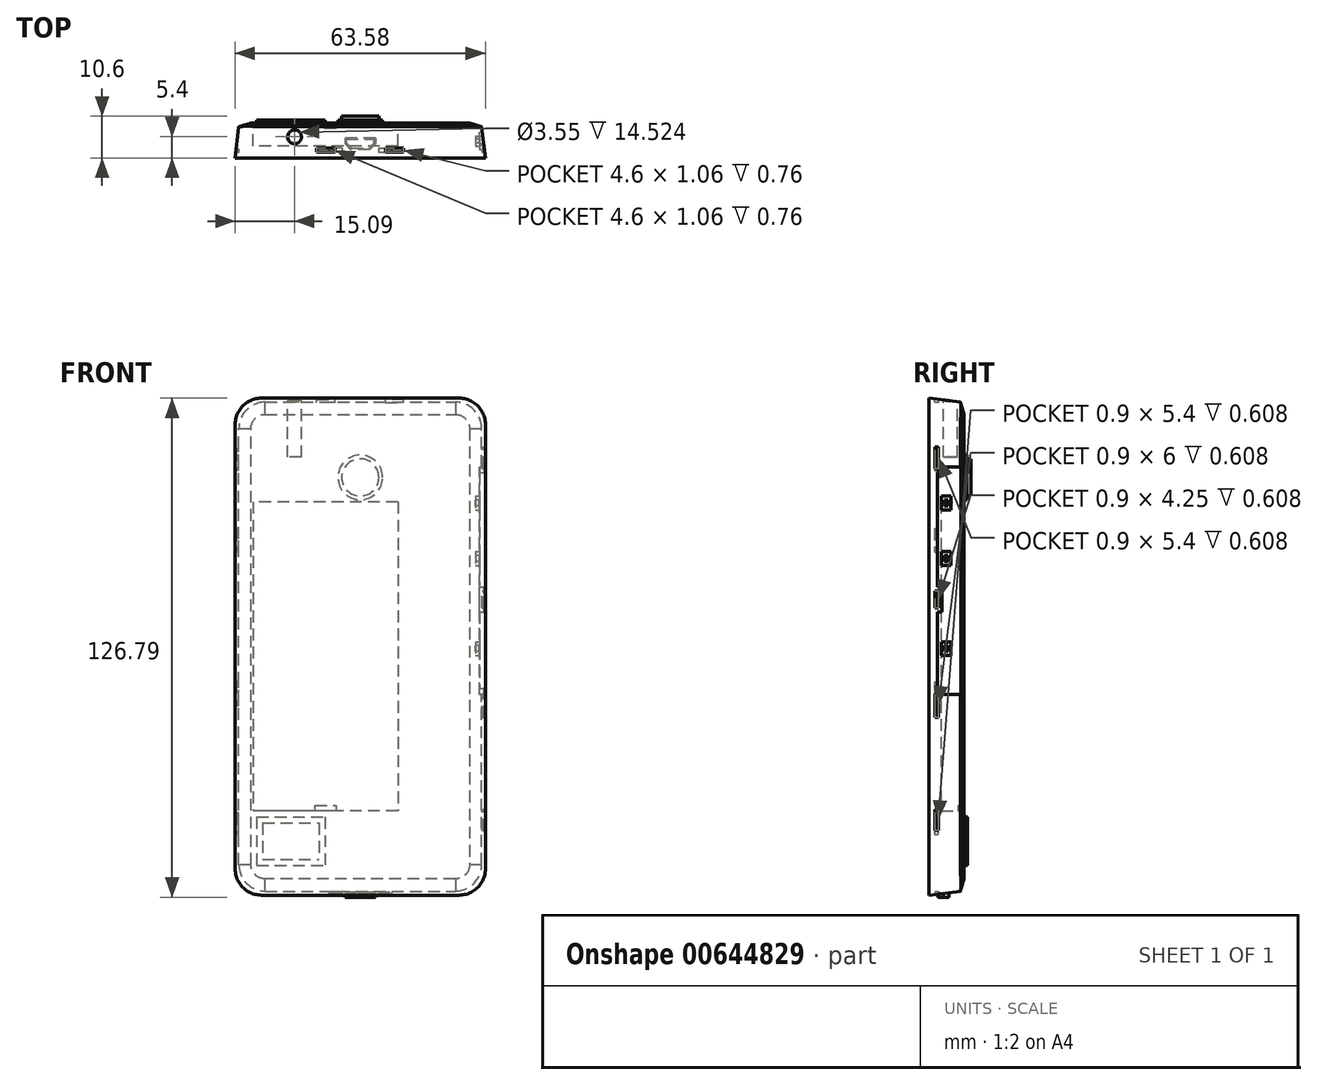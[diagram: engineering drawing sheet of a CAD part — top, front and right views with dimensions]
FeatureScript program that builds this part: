
annotation { "Feature Type Name" : "Feature", "Feature Type Description" : "" }
export const myFeature = defineFeature(function(context is Context, id is Id, definition is map)
    precondition{}
    {
        {
            var Q0;
            Q0=qCreatedBy(makeId("Front.planeOp"),FACE);
            cPlane(context, id + "F0", {"entities" : qUnion([Q0]), "cplaneType" : CPlaneType.OFFSET, "offset" : 9 * mm, "width" : 150 * mm, "height" : 150 * mm});
        }
        {
            var Q0;
            Q0=qCreatedBy(id+"F0.planeOp",FACE);
            var sketch = newSketch(context, id + "F1", { "sketchPlane" : qUnion([Q0])});
            skLineSegment(sketch, "E0.bottom", {"start": v(31.8, 63.15) * mm, "end": v(-31.8, 63.15) * mm});
            skLineSegment(sketch, "E0.top", {"start": v(31.8, -63.15) * mm, "end": v(-31.8, -63.15) * mm});
            skLineSegment(sketch, "E0.left", {"start": v(31.8, 63.15) * mm, "end": v(31.8, -63.15) * mm});
            skLineSegment(sketch, "E0.right", {"start": v(-31.8, 63.15) * mm, "end": v(-31.8, -63.15) * mm});
            skPoint(sketch, "E0.middle", {"position": v(0, 0) * mm});
            skLineSegment(sketch, "E1", {"start": v(0, -63.15) * mm, "end": v(0, -63.65) * mm, "construction": true});
            skPoint(sketch, "E1.endSnap0", {"position": v(0, -63.15) * mm});
            skSolve(sketch);
        }
        {
            var Q0;
            Q0=qCreatedBy(makeId("Front.planeOp"),FACE);
            var sketch = newSketch(context, id + "F2", { "sketchPlane" : qUnion([Q0])});
            skLineSegment(sketch, "E2.bottom", {"start": v(30.75, 62) * mm, "end": v(-30.75, 62) * mm});
            skLineSegment(sketch, "E2.top", {"start": v(30.75, -62) * mm, "end": v(-30.75, -62) * mm});
            skLineSegment(sketch, "E2.left", {"start": v(30.75, 62) * mm, "end": v(30.75, -62) * mm});
            skLineSegment(sketch, "E2.right", {"start": v(-30.75, 62) * mm, "end": v(-30.75, -62) * mm});
            skPoint(sketch, "E2.middle", {"position": v(0, 0) * mm});
            skSolve(sketch);
        }
        {
            var Q0;
            Q0=qSketchRegion(id+"F1",true);
            var Q1;
            Q1=qSketchRegion(id+"F2",true);
            loft(context, id + "F3", {"sheetProfilesArray" : [{ "sheetProfileEntities" : qUnion([Q0]) }, { "sheetProfileEntities" : qUnion([Q1]) }]});
        }
        {
            var Q0;
            Q0=makeQuery(id+"F3.opLoft","CAP_FACE",FACE,{"disambiguationData":[OSD([makeQuery(id+"F2.imprint","IMPRINT",FACE,{"disambiguationData":[TD([[makeQuery(id+"F2.imprint","IMPRINT",EDGE,{"derivedFrom":sQuery(id+"F2.wireOp",EDGE,"E2.bottom")}),1.0]])]})])],"isStart":true});
            var sketch = newSketch(context, id + "F4", { "sketchPlane" : qUnion([Q0])});
            skCircle(sketch, "E3", {"center": v(0, 43) * mm, "radius": 5.68 * mm});
            skSolve(sketch);
        }
        {
            var Q0;
            Q0=qSketchRegion(id+"F4",true);
            extrude(context, id + "F5", {"entities" : qUnion([Q0]), "operationType" : NewBodyOperationType.ADD, "depth" : 0.75 * mm});
        }
        {
            var Q0;
            Q0=makeQuery(id+"F5.opExtrude","CAP_FACE",FACE,{"disambiguationData":[OSD([sQuery(id+"F4.wireOp",EDGE,"E3")])],"isStart":false});
            var sketch = newSketch(context, id + "F6", { "sketchPlane" : qUnion([Q0])});
            skCircle(sketch, "E4", {"center": v(0, 43) * mm, "radius": 4.72 * mm});
            skSolve(sketch);
        }
        {
            var Q0;
            Q0=qSketchRegion(id+"F6",true);
            extrude(context, id + "F7", {"entities" : qUnion([Q0]), "operationType" : NewBodyOperationType.ADD, "depth" : 0.95 * mm});
        }
        {
            var Q0;
            Q0=makeQuery(id+"F3.opLoft","CAP_FACE",FACE,{"disambiguationData":[OSD([makeQuery(id+"F2.imprint","IMPRINT",FACE,{"disambiguationData":[TD([[makeQuery(id+"F2.imprint","IMPRINT",EDGE,{"derivedFrom":sQuery(id+"F2.wireOp",EDGE,"E2.bottom")}),1.0]])]})])],"isStart":true});
            var sketch = newSketch(context, id + "F8", { "sketchPlane" : qUnion([Q0])});
            skLineSegment(sketch, "E5.bottom", {"start": v(26.3, -43.3) * mm, "end": v(9, -43.3) * mm});
            skLineSegment(sketch, "E5.top", {"start": v(26.3, -55.6) * mm, "end": v(9, -55.6) * mm});
            skLineSegment(sketch, "E5.left", {"start": v(26.3, -43.3) * mm, "end": v(26.3, -55.6) * mm});
            skLineSegment(sketch, "E5.right", {"start": v(9, -43.3) * mm, "end": v(9, -55.6) * mm});
            skLineSegment(sketch, "E6", {"start": v(17.65, -43.3) * mm, "end": v(17.65, -55.6) * mm, "construction": true});
            skLineSegment(sketch, "E7.0", {"start": v(24.8, -44.8) * mm, "end": v(24.8, -54.1) * mm});
            skLineSegment(sketch, "E7.1", {"start": v(24.8, -44.8) * mm, "end": v(10.5, -44.8) * mm});
            skLineSegment(sketch, "E7.2", {"start": v(10.5, -44.8) * mm, "end": v(10.5, -54.1) * mm});
            skLineSegment(sketch, "E7.3", {"start": v(24.8, -54.1) * mm, "end": v(10.5, -54.1) * mm});
            skSolve(sketch);
        }
        {
            var Q0;
            Q0=qSketchRegion(id+"F8",true);
            extrude(context, id + "F9", {"entities" : qUnion([Q0]), "operationType" : NewBodyOperationType.ADD, "depth" : 0.78 * mm});
        }
        {
            var Q0;
            Q0=sQuery(id+"F1.wireOp",VERTEX,"E1.end");
            var Q1;
            Q1=qCreatedBy(makeId("Top.planeOp"),FACE);
            cPlane(context, id + "F10", {"entities" : qUnion([Q0, Q1]), "cplaneType" : CPlaneType.PLANE_POINT, "offset" : 25 * mm, "width" : 150 * mm, "height" : 150 * mm});
        }
        {
            var Q0;
            Q0=qCreatedBy(id+"F10.planeOp",FACE);
            var sketch = newSketch(context, id + "F11", { "sketchPlane" : qUnion([Q0])});
            skLineSegment(sketch, "E8.bottom", {"start": v(-3.85, -6.7) * mm, "end": v(-2.4, -6.7) * mm, "construction": true});
            skLineSegment(sketch, "E8.top", {"start": v(-3.85, -3.8) * mm, "end": v(3.85, -3.8) * mm});
            skLineSegment(sketch, "E8.left", {"start": v(-3.85, -6.7) * mm, "end": v(-3.85, -5.25) * mm, "construction": true});
            skLineSegment(sketch, "E8.right", {"start": v(3.84, -6.7) * mm, "end": v(3.84, -5.25) * mm, "construction": true});
            skPoint(sketch, "E8.middle", {"position": v(0, -5.25) * mm});
            skLineSegment(sketch, "E9", {"start": v(-3.85, -5.25) * mm, "end": v(-2.4, -6.7) * mm});
            skLineSegment(sketch, "E10", {"start": v(0, -3.8) * mm, "end": v(0, -6.7) * mm, "construction": true});
            skLineSegment(sketch, "E11.MirrorCS", {"start": v(3.85, -5.25) * mm, "end": v(2.4, -6.7) * mm});
            skLineSegment(sketch, "E12", {"start": v(2.4, -6.7) * mm, "end": v(3.84, -6.7) * mm, "construction": true});
            skLineSegment(sketch, "E13", {"start": v(-2.4, -6.7) * mm, "end": v(2.4, -6.7) * mm});
            skLineSegment(sketch, "E14", {"start": v(3.84, -5.25) * mm, "end": v(3.84, -3.8) * mm});
            skLineSegment(sketch, "E15", {"start": v(-3.85, -5.25) * mm, "end": v(-3.85, -3.8) * mm});
            skLineSegment(sketch, "E16.0", {"start": v(-3.51, -5.11) * mm, "end": v(-3.51, -4.13) * mm});
            skLineSegment(sketch, "E16.1", {"start": v(3.51, -5.11) * mm, "end": v(3.51, -4.13) * mm});
            skLineSegment(sketch, "E16.2", {"start": v(3.51, -5.11) * mm, "end": v(2.26, -6.37) * mm});
            skLineSegment(sketch, "E16.3", {"start": v(-3.51, -4.13) * mm, "end": v(3.51, -4.13) * mm});
            skLineSegment(sketch, "E16.4", {"start": v(-2.26, -6.37) * mm, "end": v(2.26, -6.37) * mm});
            skLineSegment(sketch, "E16.5", {"start": v(-3.51, -5.11) * mm, "end": v(-2.26, -6.37) * mm});
            skSolve(sketch);
        }
        {
            var Q0;
            Q0=qSketchRegion(id+"F11",true);
            extrude(context, id + "F12", {"entities" : qUnion([Q0]), "operationType" : NewBodyOperationType.ADD, "endBound" : BoundingType.UP_TO_NEXT, "depth" : 25 * mm});
        }
        {
            var Q0;
            Q0=qCreatedBy(makeId("Top.planeOp"),FACE);
            var Q1;
            Q1=makeQuery(id+"F3.opLoft","MID_CAP_VERTEX",VERTEX,{"disambiguationData":[OSD([sQuery(id+"F1.wireOp",EDGE,"E0.bottom"),sQuery(id+"F1.wireOp",EDGE,"E0.right")])],"capPos":0.0});
            cPlane(context, id + "F13", {"entities" : qUnion([Q0, Q1]), "cplaneType" : CPlaneType.PLANE_POINT, "offset" : 25 * mm, "width" : 150 * mm, "height" : 150 * mm});
        }
        {
            var Q0;
            Q0=qCreatedBy(id+"F13.planeOp",FACE);
            var sketch = newSketch(context, id + "F14", { "sketchPlane" : qUnion([Q0])});
            skCircle(sketch, "E17", {"center": v(-16.7, -3.5) * mm, "radius": 1.77 * mm});
            skSolve(sketch);
        }
        {
            var Q0;
            Q0=qSketchRegion(id+"F14",true);
            extrude(context, id + "F15", {"entities" : qUnion([Q0]), "operationType" : NewBodyOperationType.REMOVE, "oppositeDirection" : true, "depth" : 15 * mm});
        }
        {
            var Q0;
            {var subQ6=sQuery(id+"F2.wireOp",EDGE,"E2.bottom");Q0=makeQuery(id+"F9.boolean.opBoolean","SPLIT",FACE,{"disambiguationData":[TD([makeQuery(id+"F5.opExtrude","SWEPT_FACE",FACE,{"disambiguationData":[OSD([sQuery(id+"F4.wireOp",EDGE,"E3")])]})])],"derivedFrom":makeQuery(id+"F3.opLoft","CAP_FACE",FACE,{"disambiguationData":[OSD([makeQuery(id+"F2.imprint","IMPRINT",FACE,{"disambiguationData":[TD([[makeQuery(id+"F2.imprint","IMPRINT",EDGE,{"derivedFrom":subQ6}),1.0]])]})])],"isStart":true})});}
            var sketch = newSketch(context, id + "F16", { "sketchPlane" : qUnion([Q0])});
            skLineSegment(sketch, "E18.bottom", {"start": v(-9.56, 36.8) * mm, "end": v(27.24, 36.8) * mm});
            skLineSegment(sketch, "E18.top", {"start": v(-9.56, -41.73) * mm, "end": v(27.24, -41.73) * mm});
            skLineSegment(sketch, "E18.left", {"start": v(-9.56, 36.8) * mm, "end": v(-9.56, -41.73) * mm});
            skLineSegment(sketch, "E18.right", {"start": v(27.24, 36.8) * mm, "end": v(27.24, -41.73) * mm});
            skSolve(sketch);
        }
        {
            var Q0;
            Q0=qSketchRegion(id+"F16",true);
            extrude(context, id + "F17", {"entities" : qUnion([Q0]), "operationType" : NewBodyOperationType.REMOVE, "oppositeDirection" : true, "depth" : 5.84 * mm});
        }
        {
            var Q0;
            {var subQ6=sQuery(id+"F2.wireOp",EDGE,"E2.bottom");Q0=makeQuery(id+"F9.boolean.opBoolean","SPLIT",FACE,{"disambiguationData":[TD([makeQuery(id+"F5.opExtrude","SWEPT_FACE",FACE,{"disambiguationData":[OSD([sQuery(id+"F4.wireOp",EDGE,"E3")])]})])],"derivedFrom":makeQuery(id+"F3.opLoft","CAP_FACE",FACE,{"disambiguationData":[OSD([makeQuery(id+"F2.imprint","IMPRINT",FACE,{"disambiguationData":[TD([[makeQuery(id+"F2.imprint","IMPRINT",EDGE,{"derivedFrom":subQ6}),1.0]])]})])],"isStart":true})});}
            var sketch = newSketch(context, id + "F18", { "sketchPlane" : qUnion([Q0])});
            skLineSegment(sketch, "E19.0", {"start": v(6.2, -41.73) * mm, "end": v(11.5, -41.73) * mm});
            skLineSegment(sketch, "E20", {"start": v(11.5, -41.73) * mm, "end": v(11.5, -40.33) * mm});
            skLineSegment(sketch, "E21", {"start": v(11.5, -40.33) * mm, "end": v(6.2, -40.33) * mm});
            skLineSegment(sketch, "E22", {"start": v(6.2, -40.33) * mm, "end": v(6.2, -41.73) * mm});
            skPoint(sketch, "E23.orphan", {"position": v(-9.56, -41.73) * mm});
            skPoint(sketch, "E24.orphan", {"position": v(27.24, -41.73) * mm});
            skLineSegment(sketch, "E25", {"start": v(8.84, -40.33) * mm, "end": v(8.84, -41.73) * mm, "construction": true});
            skSolve(sketch);
        }
        {
            var Q0;
            Q0=qSketchRegion(id+"F18",true);
            extrude(context, id + "F19", {"entities" : qUnion([Q0]), "operationType" : NewBodyOperationType.ADD, "oppositeDirection" : true, "depth" : 1.4 * mm});
        }
        {
            var Q0;
            Q0=qCreatedBy(makeId("Right.planeOp"),FACE);
            var Q1;
            Q1=makeQuery(id+"F3.opLoft","MID_CAP_VERTEX",VERTEX,{"disambiguationData":[OSD([sQuery(id+"F1.wireOp",EDGE,"E0.bottom"),sQuery(id+"F1.wireOp",EDGE,"E0.left")])],"capPos":0.0});
            cPlane(context, id + "F20", {"entities" : qUnion([Q0, Q1]), "cplaneType" : CPlaneType.PLANE_POINT, "offset" : 25 * mm, "width" : 150 * mm, "height" : 150 * mm});
        }
        {
            var Q0;
            Q0=qCreatedBy(id+"F20.planeOp",FACE);
            var sketch = newSketch(context, id + "F21", { "sketchPlane" : qUnion([Q0])});
            skLineSegment(sketch, "E26.0", {"start": v(0, 62) * mm, "end": v(0, -62) * mm});
            skLineSegment(sketch, "E27", {"start": v(0, 45.7) * mm, "end": v(-5.28, 45.7) * mm});
            skLineSegment(sketch, "E28", {"start": v(-6.78, 44.2) * mm, "end": v(-6.78, 15.2) * mm});
            skLineSegment(sketch, "E29", {"start": v(-5.28, -12.1) * mm, "end": v(0, -12.1) * mm});
            skLineSegment(sketch, "E30", {"start": v(-5.28, 45.7) * mm, "end": v(-6.78, 44.2) * mm});
            skLineSegment(sketch, "E31", {"start": v(-5.28, -12.1) * mm, "end": v(-6.78, -10.6) * mm});
            skLineSegment(sketch, "E32", {"start": v(-6.78, 8.8) * mm, "end": v(-5.67, 8.8) * mm});
            skLineSegment(sketch, "E33", {"start": v(-5.67, 8.8) * mm, "end": v(-5.67, 15.2) * mm});
            skLineSegment(sketch, "E34", {"start": v(-5.67, 15.2) * mm, "end": v(-6.78, 15.2) * mm});
            skPoint(sketch, "E35", {"position": v(-5.67, 12) * mm});
            skLineSegment(sketch, "E36.trimOffspring", {"start": v(-6.78, 8.8) * mm, "end": v(-6.78, -10.6) * mm});
            skSolve(sketch);
        }
        {
            var Q0;
            Q0=qSketchRegion(id+"F21",true);
            extrude(context, id + "F22", {"entities" : qUnion([Q0]), "operationType" : NewBodyOperationType.REMOVE, "oppositeDirection" : true, "depth" : 1.5 * mm});
        }
        {
            var Q0;
            Q0=makeQuery(id+"F22.boolean.opBoolean","COPY",FACE,{"derivedFrom":makeQuery(id+"F22.opExtrude","CAP_FACE",FACE,{"disambiguationData":[OSD([sQuery(id+"F21.wireOp",EDGE,"E26.0"),sQuery(id+"F21.wireOp",EDGE,"E27"),sQuery(id+"F21.wireOp",EDGE,"E28"),sQuery(id+"F21.wireOp",EDGE,"E29")])],"isStart":false})});
            var sketch = newSketch(context, id + "F23", { "sketchPlane" : qUnion([Q0])});
            skLineSegment(sketch, "E37.bottom", {"start": v(-3.3, 38.25) * mm, "end": v(-5.8, 38.25) * mm});
            skLineSegment(sketch, "E37.top", {"start": v(-3.3, 34.75) * mm, "end": v(-5.8, 34.75) * mm});
            skLineSegment(sketch, "E37.left", {"start": v(-3.3, 38.25) * mm, "end": v(-3.3, 34.75) * mm});
            skLineSegment(sketch, "E37.right", {"start": v(-5.8, 38.25) * mm, "end": v(-5.8, 34.75) * mm});
            skLineSegment(sketch, "E38.bottom", {"start": v(-3.3, 24.15) * mm, "end": v(-5.8, 24.15) * mm});
            skLineSegment(sketch, "E38.top", {"start": v(-3.3, 20.65) * mm, "end": v(-5.8, 20.65) * mm});
            skLineSegment(sketch, "E38.left", {"start": v(-3.3, 24.15) * mm, "end": v(-3.3, 20.65) * mm});
            skLineSegment(sketch, "E38.right", {"start": v(-5.8, 24.15) * mm, "end": v(-5.8, 20.65) * mm});
            skLineSegment(sketch, "E39.bottom", {"start": v(-3.3, 1.25) * mm, "end": v(-5.8, 1.25) * mm});
            skLineSegment(sketch, "E39.top", {"start": v(-3.3, -2.25) * mm, "end": v(-5.8, -2.25) * mm});
            skLineSegment(sketch, "E39.left", {"start": v(-3.3, 1.25) * mm, "end": v(-3.3, -2.25) * mm});
            skLineSegment(sketch, "E39.right", {"start": v(-5.8, 1.25) * mm, "end": v(-5.8, -2.25) * mm});
            skLineSegment(sketch, "E40", {"start": v(-3.3, 36.5) * mm, "end": v(-5.8, 36.5) * mm, "construction": true});
            skLineSegment(sketch, "E41", {"start": v(-3.3, 22.4) * mm, "end": v(-5.8, 22.4) * mm, "construction": true});
            skLineSegment(sketch, "E42", {"start": v(-3.3, -0.5) * mm, "end": v(-5.8, -0.5) * mm, "construction": true});
            skSolve(sketch);
        }
        {
            var Q0;
            Q0=qSketchRegion(id+"F23",true);
            extrude(context, id + "F24", {"entities" : qUnion([Q0]), "operationType" : NewBodyOperationType.REMOVE, "oppositeDirection" : true, "depth" : 1 * mm});
        }
        {
            var Q0;
            Q0=makeQuery(id+"F24.boolean.opBoolean","COPY",FACE,{"derivedFrom":makeQuery(id+"F24.opExtrude","CAP_FACE",FACE,{"disambiguationData":[OSD([sQuery(id+"F23.wireOp",EDGE,"E37.bottom"),sQuery(id+"F23.wireOp",EDGE,"E37.top"),sQuery(id+"F23.wireOp",EDGE,"E37.left"),sQuery(id+"F23.wireOp",EDGE,"E37.right")])],"isStart":false})});
            var sketch = newSketch(context, id + "F25", { "sketchPlane" : qUnion([Q0])});
            skLineSegment(sketch, "E43.bottom", {"start": v(-4.05, 35.75) * mm, "end": v(-5.05, 35.75) * mm});
            skLineSegment(sketch, "E43.top", {"start": v(-4.05, 37.25) * mm, "end": v(-5.05, 37.25) * mm});
            skLineSegment(sketch, "E43.left", {"start": v(-4.05, 35.75) * mm, "end": v(-4.05, 37.25) * mm});
            skLineSegment(sketch, "E43.right", {"start": v(-5.05, 35.75) * mm, "end": v(-5.05, 37.25) * mm});
            skPoint(sketch, "E43.middle", {"position": v(-4.55, 36.5) * mm});
            skPoint(sketch, "E43.middle.positionSnap0", {"position": v(-3.3, 36.5) * mm});
            skPoint(sketch, "E43.middle.positionSnap1", {"position": v(-4.55, 34.75) * mm});
            skPoint(sketch, "E43.centerSnap0", {"position": v(-3.3, 36.5) * mm});
            skPoint(sketch, "E43.centerSnap1", {"position": v(-4.55, 34.75) * mm});
            skPoint(sketch, "E44.0", {"position": v(-3.3, 22.4) * mm});
            skPoint(sketch, "E45.0", {"position": v(-3.3, -0.5) * mm});
            skLineSegment(sketch, "E46.bottom", {"start": v(-4.05, 23.15) * mm, "end": v(-5.05, 23.15) * mm});
            skLineSegment(sketch, "E46.top", {"start": v(-4.05, 21.65) * mm, "end": v(-5.05, 21.65) * mm});
            skLineSegment(sketch, "E46.left", {"start": v(-4.05, 23.15) * mm, "end": v(-4.05, 21.65) * mm});
            skLineSegment(sketch, "E46.right", {"start": v(-5.05, 23.15) * mm, "end": v(-5.05, 21.65) * mm});
            skPoint(sketch, "E46.middle", {"position": v(-4.55, 22.4) * mm});
            skLineSegment(sketch, "E47.bottom", {"start": v(-4.05, -1.25) * mm, "end": v(-5.05, -1.25) * mm});
            skLineSegment(sketch, "E47.top", {"start": v(-4.05, 0.25) * mm, "end": v(-5.05, 0.25) * mm});
            skLineSegment(sketch, "E47.left", {"start": v(-4.05, -1.25) * mm, "end": v(-4.05, 0.25) * mm});
            skLineSegment(sketch, "E47.right", {"start": v(-5.05, -1.25) * mm, "end": v(-5.05, 0.25) * mm});
            skPoint(sketch, "E47.middle", {"position": v(-4.55, -0.5) * mm});
            skSolve(sketch);
        }
        {
            var Q0;
            Q0=qSketchRegion(id+"F25",true);
            extrude(context, id + "F26", {"entities" : qUnion([Q0]), "operationType" : NewBodyOperationType.ADD, "depth" : 0.85 * mm});
        }
        {
            var Q0;
            Q0=qCreatedBy(id+"F20.planeOp",FACE);
            var sketch = newSketch(context, id + "F27", { "sketchPlane" : qUnion([Q0])});
            skLineSegment(sketch, "E48.bottom", {"start": v(-6.5, 45.3) * mm, "end": v(-7.4, 45.3) * mm});
            skLineSegment(sketch, "E48.top", {"start": v(-6.5, 50.7) * mm, "end": v(-7.4, 50.7) * mm});
            skLineSegment(sketch, "E48.left", {"start": v(-6.5, 45.3) * mm, "end": v(-6.5, 50.7) * mm});
            skLineSegment(sketch, "E48.right", {"start": v(-7.4, 45.3) * mm, "end": v(-7.4, 50.7) * mm});
            skPoint(sketch, "E48.middle", {"position": v(-6.95, 48) * mm});
            skLineSegment(sketch, "E49.bottom", {"start": v(-6.5, 9.87) * mm, "end": v(-7.4, 9.87) * mm});
            skLineSegment(sketch, "E49.top", {"start": v(-6.5, 14.12) * mm, "end": v(-7.4, 14.12) * mm});
            skLineSegment(sketch, "E49.left", {"start": v(-6.5, 9.87) * mm, "end": v(-6.5, 14.12) * mm});
            skLineSegment(sketch, "E49.right", {"start": v(-7.4, 9.87) * mm, "end": v(-7.4, 14.12) * mm});
            skPoint(sketch, "E49.middle", {"position": v(-6.95, 12) * mm});
            skLineSegment(sketch, "E50.bottom", {"start": v(-6.5, -18) * mm, "end": v(-7.4, -18) * mm});
            skLineSegment(sketch, "E50.top", {"start": v(-6.5, -12) * mm, "end": v(-7.4, -12) * mm});
            skLineSegment(sketch, "E50.left", {"start": v(-6.5, -18) * mm, "end": v(-6.5, -12) * mm});
            skLineSegment(sketch, "E50.right", {"start": v(-7.4, -18) * mm, "end": v(-7.4, -12) * mm});
            skPoint(sketch, "E50.middle", {"position": v(-6.95, -15) * mm});
            skLineSegment(sketch, "E51.bottom", {"start": v(-6.5, -46.7) * mm, "end": v(-7.4, -46.7) * mm});
            skLineSegment(sketch, "E51.top", {"start": v(-6.5, -41.3) * mm, "end": v(-7.4, -41.3) * mm});
            skLineSegment(sketch, "E51.left", {"start": v(-6.5, -46.7) * mm, "end": v(-6.5, -41.3) * mm});
            skLineSegment(sketch, "E51.right", {"start": v(-7.4, -46.7) * mm, "end": v(-7.4, -41.3) * mm});
            skPoint(sketch, "E51.middle", {"position": v(-6.95, -44) * mm});
            skSolve(sketch);
        }
        {
            var Q0;
            Q0=qSketchRegion(id+"F27",true);
            extrude(context, id + "F28", {"entities" : qUnion([Q0]), "operationType" : NewBodyOperationType.REMOVE, "oppositeDirection" : true, "depth" : 0.9 * mm});
        }
        {
            var Q0;
            Q0=qCreatedBy(makeId("Right.planeOp"),FACE);
            var Q1;
            Q1=makeQuery(id+"F3.opLoft","MID_CAP_VERTEX",VERTEX,{"disambiguationData":[OSD([sQuery(id+"F1.wireOp",EDGE,"E0.bottom"),sQuery(id+"F1.wireOp",EDGE,"E0.right")])],"capPos":0.0});
            cPlane(context, id + "F29", {"entities" : qUnion([Q0, Q1]), "cplaneType" : CPlaneType.PLANE_POINT, "offset" : 25 * mm, "width" : 150 * mm, "height" : 150 * mm});
        }
        {
            var Q0;
            Q0=qCreatedBy(id+"F29.planeOp",FACE);
            var sketch = newSketch(context, id + "F30", { "sketchPlane" : qUnion([Q0])});
            skLineSegment(sketch, "E52.bottom", {"start": v(-6.6, 44.8) * mm, "end": v(-7.5, 44.8) * mm});
            skLineSegment(sketch, "E52.top", {"start": v(-6.6, 50.2) * mm, "end": v(-7.5, 50.2) * mm});
            skLineSegment(sketch, "E52.left", {"start": v(-6.6, 44.8) * mm, "end": v(-6.6, 50.2) * mm});
            skLineSegment(sketch, "E52.right", {"start": v(-7.5, 44.8) * mm, "end": v(-7.5, 50.2) * mm});
            skPoint(sketch, "E52.middle", {"position": v(-7.05, 47.5) * mm});
            skLineSegment(sketch, "E53.bottom", {"start": v(-6.6, 24) * mm, "end": v(-7.5, 24) * mm});
            skLineSegment(sketch, "E53.top", {"start": v(-6.6, 30) * mm, "end": v(-7.5, 30) * mm});
            skLineSegment(sketch, "E53.left", {"start": v(-6.6, 24) * mm, "end": v(-6.6, 30) * mm});
            skLineSegment(sketch, "E53.right", {"start": v(-7.5, 24) * mm, "end": v(-7.5, 30) * mm});
            skPoint(sketch, "E53.middle", {"position": v(-7.05, 27) * mm});
            skLineSegment(sketch, "E54.bottom", {"start": v(-6.6, -15.05) * mm, "end": v(-7.5, -15.05) * mm});
            skLineSegment(sketch, "E54.top", {"start": v(-6.6, -8.95) * mm, "end": v(-7.5, -8.95) * mm});
            skLineSegment(sketch, "E54.left", {"start": v(-6.6, -15.05) * mm, "end": v(-6.6, -8.95) * mm});
            skLineSegment(sketch, "E54.right", {"start": v(-7.5, -15.05) * mm, "end": v(-7.5, -8.95) * mm});
            skPoint(sketch, "E54.middle", {"position": v(-7.05, -12) * mm});
            skPoint(sketch, "E54.middle.positionSnap0", {"position": v(-7.05, 24) * mm});
            skPoint(sketch, "E54.cornerSnap0", {"position": v(-6.6, 47.5) * mm});
            skPoint(sketch, "E54.centerSnap0", {"position": v(-7.05, 24) * mm});
            skLineSegment(sketch, "E55.bottom", {"start": v(-6.6, -47.75) * mm, "end": v(-7.5, -47.75) * mm});
            skLineSegment(sketch, "E55.top", {"start": v(-6.6, -42.25) * mm, "end": v(-7.5, -42.25) * mm});
            skLineSegment(sketch, "E55.left", {"start": v(-6.6, -47.75) * mm, "end": v(-6.6, -42.25) * mm});
            skLineSegment(sketch, "E55.right", {"start": v(-7.5, -47.75) * mm, "end": v(-7.5, -42.25) * mm});
            skPoint(sketch, "E55.middle", {"position": v(-7.05, -45) * mm});
            skSolve(sketch);
        }
        {
            var Q0;
            Q0=qSketchRegion(id+"F30",true);
            extrude(context, id + "F31", {"entities" : qUnion([Q0]), "operationType" : NewBodyOperationType.REMOVE, "depth" : 0.9 * mm});
        }
        {
            var Q0;
            Q0=qCreatedBy(makeId("Top.planeOp"),FACE);
            var Q1;
            Q1=makeQuery(id+"F3.opLoft","MID_CAP_VERTEX",VERTEX,{"disambiguationData":[OSD([sQuery(id+"F1.wireOp",EDGE,"E0.top"),sQuery(id+"F1.wireOp",EDGE,"E0.right")])],"capPos":0.0});
            cPlane(context, id + "F32", {"entities" : qUnion([Q0, Q1]), "cplaneType" : CPlaneType.PLANE_POINT, "offset" : 25 * mm, "width" : 150 * mm, "height" : 150 * mm});
        }
        {
            var Q0;
            Q0=qCreatedBy(id+"F32.planeOp",FACE);
            var sketch = newSketch(context, id + "F33", { "sketchPlane" : qUnion([Q0])});
            skLineSegment(sketch, "E56.bottom", {"start": v(4.6, -6.37) * mm, "end": v(7.9, -6.37) * mm});
            skLineSegment(sketch, "E56.top", {"start": v(4.6, -7.37) * mm, "end": v(7.9, -7.37) * mm});
            skLineSegment(sketch, "E56.left", {"start": v(4.6, -6.37) * mm, "end": v(4.6, -7.37) * mm});
            skLineSegment(sketch, "E56.right", {"start": v(7.9, -6.37) * mm, "end": v(7.9, -7.37) * mm});
            skPoint(sketch, "E56.middle", {"position": v(6.25, -6.87) * mm});
            skPoint(sketch, "E57.0", {"position": v(0, 0) * mm});
            skLineSegment(sketch, "E58", {"start": v(0, 0) * mm, "end": v(0, -3.54) * mm, "construction": true});
            skPoint(sketch, "E59.MirrorP", {"position": v(-6.25, -6.87) * mm});
            skLineSegment(sketch, "E60.MirrorCS", {"start": v(-4.6, -6.37) * mm, "end": v(-4.6, -7.37) * mm});
            skLineSegment(sketch, "E61.MirrorCS", {"start": v(-7.9, -6.37) * mm, "end": v(-7.9, -7.37) * mm});
            skLineSegment(sketch, "E62.MirrorCS", {"start": v(-4.6, -7.37) * mm, "end": v(-7.9, -7.37) * mm});
            skLineSegment(sketch, "E63.MirrorCS", {"start": v(-4.6, -6.37) * mm, "end": v(-7.9, -6.37) * mm});
            skSolve(sketch);
        }
        {
            var Q0;
            Q0=qSketchRegion(id+"F33",true);
            extrude(context, id + "F34", {"entities" : qUnion([Q0]), "operationType" : NewBodyOperationType.REMOVE, "depth" : .9 * mm});
        }
        {
            var Q0;
            Q0=qCreatedBy(makeId("Top.planeOp"),FACE);
            var Q1;
            Q1=makeQuery(id+"F3.opLoft","MID_CAP_VERTEX",VERTEX,{"disambiguationData":[OSD([sQuery(id+"F1.wireOp",EDGE,"E0.bottom"),sQuery(id+"F1.wireOp",EDGE,"E0.left")])],"capPos":0.0});
            cPlane(context, id + "F35", {"entities" : qUnion([Q0, Q1]), "cplaneType" : CPlaneType.PLANE_POINT, "offset" : 25 * mm, "width" : 150 * mm, "height" : 150 * mm});
        }
        {
            var Q0;
            Q0=qCreatedBy(id+"F35.planeOp",FACE);
            var sketch = newSketch(context, id + "F36", { "sketchPlane" : qUnion([Q0])});
            skLineSegment(sketch, "E64.bottom", {"start": v(-6.45, -6.34) * mm, "end": v(-11.05, -6.34) * mm});
            skLineSegment(sketch, "E64.top", {"start": v(-6.45, -7.4) * mm, "end": v(-11.05, -7.4) * mm});
            skLineSegment(sketch, "E64.left", {"start": v(-6.45, -6.34) * mm, "end": v(-6.45, -7.4) * mm});
            skLineSegment(sketch, "E64.right", {"start": v(-11.05, -6.34) * mm, "end": v(-11.05, -7.4) * mm});
            skPoint(sketch, "E64.middle", {"position": v(-8.75, -6.87) * mm});
            skLineSegment(sketch, "E65", {"start": v(0, 0) * mm, "end": v(0, -6.87) * mm, "construction": true});
            skPoint(sketch, "E66.MirrorP", {"position": v(8.75, -6.87) * mm});
            skLineSegment(sketch, "E67.MirrorCS", {"start": v(6.45, -6.34) * mm, "end": v(11.05, -6.34) * mm});
            skLineSegment(sketch, "E68.MirrorCS", {"start": v(6.45, -6.34) * mm, "end": v(6.45, -7.4) * mm});
            skLineSegment(sketch, "E69.MirrorCS", {"start": v(11.05, -6.34) * mm, "end": v(11.05, -7.4) * mm});
            skLineSegment(sketch, "E70.MirrorCS", {"start": v(6.45, -7.4) * mm, "end": v(11.05, -7.4) * mm});
            skSolve(sketch);
        }
        {
            var Q0;
            Q0=qSketchRegion(id+"F36",true);
            extrude(context, id + "F37", {"entities" : qUnion([Q0]), "operationType" : NewBodyOperationType.REMOVE, "oppositeDirection" : true, "depth" : 1.1 * mm});
        }
        {
            var Q0;
            Q0=makeQuery(id+"F3.opLoft","SWEPT_EDGE",EDGE,{"disambiguationData":[OSD([sQuery(id+"F1.wireOp",EDGE,"E0.bottom"),sQuery(id+"F1.wireOp",EDGE,"E0.left"),sQuery(id+"F2.wireOp",EDGE,"E2.bottom"),sQuery(id+"F2.wireOp",EDGE,"E2.left")])]});
            var Q1;
            Q1=makeQuery(id+"F3.opLoft","SWEPT_EDGE",EDGE,{"disambiguationData":[OSD([sQuery(id+"F1.wireOp",EDGE,"E0.bottom"),sQuery(id+"F1.wireOp",EDGE,"E0.right"),sQuery(id+"F2.wireOp",EDGE,"E2.bottom"),sQuery(id+"F2.wireOp",EDGE,"E2.right")])]});
            var Q2;
            Q2=makeQuery(id+"F3.opLoft","SWEPT_EDGE",EDGE,{"disambiguationData":[OSD([sQuery(id+"F1.wireOp",EDGE,"E0.top"),sQuery(id+"F1.wireOp",EDGE,"E0.left"),sQuery(id+"F2.wireOp",EDGE,"E2.top"),sQuery(id+"F2.wireOp",EDGE,"E2.left")])]});
            var Q3;
            Q3=makeQuery(id+"F3.opLoft","SWEPT_EDGE",EDGE,{"disambiguationData":[OSD([sQuery(id+"F1.wireOp",EDGE,"E0.top"),sQuery(id+"F1.wireOp",EDGE,"E0.right"),sQuery(id+"F2.wireOp",EDGE,"E2.top"),sQuery(id+"F2.wireOp",EDGE,"E2.right")])]});
            fillet(context, id + "F38", {"entities" : qUnion([Q0, Q1, Q2, Q3]), "radius" : 6.75 * mm, "tangentPropagation" : true, "allowEdgeOverflow" : false});
        }
        {
            var Q0;
            Q0=makeQuery(id+"F3.opLoft","MID_CAP_EDGE",EDGE,{"disambiguationData":[OSD([sQuery(id+"F2.wireOp",EDGE,"E2.bottom"),sQuery(id+"F2.wireOp",EDGE,"E2.top"),sQuery(id+"F2.wireOp",EDGE,"E2.right")])],"capPos":1.0});
            chamfer(context, id + "F39", {"entities" : qUnion([Q0]), "chamferType" : ChamferType.TWO_OFFSETS, "width1" : 3 * mm, "oppositeDirection" : false, "width2" : 1 * mm, "tangentPropagation" : true});
        }
        {
            var Q0;
            Q0=makeQuery(id+"F3.opLoft","CAP_FACE",FACE,{"disambiguationData":[OSD([makeQuery(id+"F1.imprint","IMPRINT",FACE,{"disambiguationData":[TD([[makeQuery(id+"F1.imprint","IMPRINT",EDGE,{"derivedFrom":sQuery(id+"F1.wireOp",EDGE,"E0.bottom")}),1.0]])]})])],"isStart":true});
            var sketch = newSketch(context, id + "F40", { "sketchPlane" : qUnion([Q0])});
            skFitSpline(sketch, "E71.0", {"points": [v(-21.84, 51.15) * mm, v(-20.9, 51.85) * mm, v(-20.11, 52.72) * mm, v(-19.52, 53.73) * mm, v(-19.13, 54.85) * mm, v(-18.97, 56.01) * mm, v(-19.04, 57.2) * mm, v(-19.35, 58.35) * mm, v(-19.86, 59.42) * mm, v(-20.58, 60.38) * mm, v(-21.47, 61.19) * mm, v(-22.5, 61.8) * mm, v(-23.62, 62.2) * mm, v(-24.79, 62.38) * mm, v(-25.96, 62.33) * mm, v(-27.11, 62.04) * mm, v(-28.17, 61.54) * mm, v(-29.11, 60.84) * mm, v(-29.9, 59.97) * mm, v(-30.49, 58.96) * mm, v(-30.87, 57.84) * mm, v(-31.03, 56.68) * mm, v(-30.96, 55.5) * mm, v(-30.66, 54.34) * mm, v(-30.14, 53.27) * mm, v(-29.43, 52.3) * mm, v(-28.54, 51.5) * mm, v(-27.52, 50.9) * mm, v(-26.4, 50.49) * mm, v(-25.22, 50.31) * mm, v(-24.04, 50.36) * mm, v(-22.9, 50.65) * mm, v(-21.84, 51.15) * mm, v(-20.9, 51.85) * mm, v(-20.11, 52.72) * mm]});
            skLineSegment(sketch, "E71.1", {"start": v(-31, -56.45) * mm, "end": v(-31, 56.45) * mm});
            skLineSegment(sketch, "E71.2", {"start": v(-25.1, 62.35) * mm, "end": v(25.1, 62.35) * mm});
            skFitSpline(sketch, "E71.3", {"points": [v(-29.9, -59.97) * mm, v(-29.11, -60.84) * mm, v(-28.17, -61.54) * mm, v(-27.11, -62.04) * mm, v(-25.96, -62.33) * mm, v(-24.79, -62.38) * mm, v(-23.62, -62.2) * mm, v(-22.5, -61.8) * mm, v(-21.47, -61.19) * mm, v(-20.58, -60.38) * mm, v(-19.86, -59.42) * mm, v(-19.35, -58.35) * mm, v(-19.04, -57.2) * mm, v(-18.97, -56.01) * mm, v(-19.13, -54.85) * mm, v(-19.52, -53.73) * mm, v(-20.11, -52.72) * mm, v(-20.9, -51.85) * mm, v(-21.84, -51.15) * mm, v(-22.9, -50.65) * mm, v(-24.04, -50.36) * mm, v(-25.22, -50.31) * mm, v(-26.4, -50.49) * mm, v(-27.52, -50.9) * mm, v(-28.54, -51.5) * mm, v(-29.43, -52.3) * mm, v(-30.14, -53.27) * mm, v(-30.66, -54.34) * mm, v(-30.96, -55.5) * mm, v(-31.03, -56.68) * mm, v(-30.87, -57.84) * mm, v(-30.49, -58.96) * mm, v(-29.9, -59.97) * mm, v(-29.11, -60.84) * mm, v(-28.17, -61.54) * mm]});
            skFitSpline(sketch, "E71.4", {"points": [v(29.9, 59.97) * mm, v(29.11, 60.84) * mm, v(28.17, 61.54) * mm, v(27.11, 62.04) * mm, v(25.96, 62.33) * mm, v(24.79, 62.38) * mm, v(23.62, 62.2) * mm, v(22.5, 61.8) * mm, v(21.47, 61.19) * mm, v(20.58, 60.38) * mm, v(19.86, 59.42) * mm, v(19.35, 58.35) * mm, v(19.04, 57.2) * mm, v(18.97, 56.01) * mm, v(19.13, 54.85) * mm, v(19.52, 53.73) * mm, v(20.11, 52.72) * mm, v(20.9, 51.85) * mm, v(21.84, 51.15) * mm, v(22.9, 50.65) * mm, v(24.04, 50.36) * mm, v(25.22, 50.31) * mm, v(26.4, 50.49) * mm, v(27.52, 50.9) * mm, v(28.54, 51.5) * mm, v(29.43, 52.3) * mm, v(30.14, 53.27) * mm, v(30.66, 54.34) * mm, v(30.96, 55.5) * mm, v(31.03, 56.68) * mm, v(30.87, 57.84) * mm, v(30.49, 58.96) * mm, v(29.9, 59.97) * mm, v(29.11, 60.84) * mm, v(28.17, 61.54) * mm]});
            skLineSegment(sketch, "E71.5", {"start": v(31, -56.45) * mm, "end": v(31, 56.45) * mm});
            skFitSpline(sketch, "E71.6", {"points": [v(21.84, -51.15) * mm, v(20.9, -51.85) * mm, v(20.11, -52.72) * mm, v(19.52, -53.73) * mm, v(19.13, -54.85) * mm, v(18.97, -56.01) * mm, v(19.04, -57.2) * mm, v(19.35, -58.35) * mm, v(19.86, -59.42) * mm, v(20.58, -60.38) * mm, v(21.47, -61.19) * mm, v(22.5, -61.8) * mm, v(23.62, -62.2) * mm, v(24.79, -62.38) * mm, v(25.96, -62.33) * mm, v(27.11, -62.04) * mm, v(28.17, -61.54) * mm, v(29.11, -60.84) * mm, v(29.9, -59.97) * mm, v(30.49, -58.96) * mm, v(30.87, -57.84) * mm, v(31.03, -56.68) * mm, v(30.96, -55.5) * mm, v(30.66, -54.34) * mm, v(30.14, -53.27) * mm, v(29.43, -52.3) * mm, v(28.54, -51.5) * mm, v(27.52, -50.9) * mm, v(26.4, -50.49) * mm, v(25.22, -50.31) * mm, v(24.04, -50.36) * mm, v(22.9, -50.65) * mm, v(21.84, -51.15) * mm, v(20.9, -51.85) * mm, v(20.11, -52.72) * mm]});
            skLineSegment(sketch, "E71.7", {"start": v(-25.1, -62.35) * mm, "end": v(25.1, -62.35) * mm});
            skLineSegment(sketch, "E72.bottom", {"start": v(37.5, 67.5) * mm, "end": v(-37.5, 67.5) * mm});
            skLineSegment(sketch, "E72.top", {"start": v(37.5, -67.5) * mm, "end": v(-37.5, -67.5) * mm});
            skLineSegment(sketch, "E72.left", {"start": v(37.5, 67.5) * mm, "end": v(37.5, -67.5) * mm});
            skLineSegment(sketch, "E72.right", {"start": v(-37.5, 67.5) * mm, "end": v(-37.5, -67.5) * mm});
            skPoint(sketch, "E72.middle", {"position": v(0, 0) * mm});
            skSolve(sketch);
        }
        {
            var Q0;
            Q0=qSketchRegion(id+"F40",true);
            extrude(context, id + "F41", {"entities" : qUnion([Q0]), "operationType" : NewBodyOperationType.REMOVE, "oppositeDirection" : true, "depth" : .1 * mm});
        }
    });
